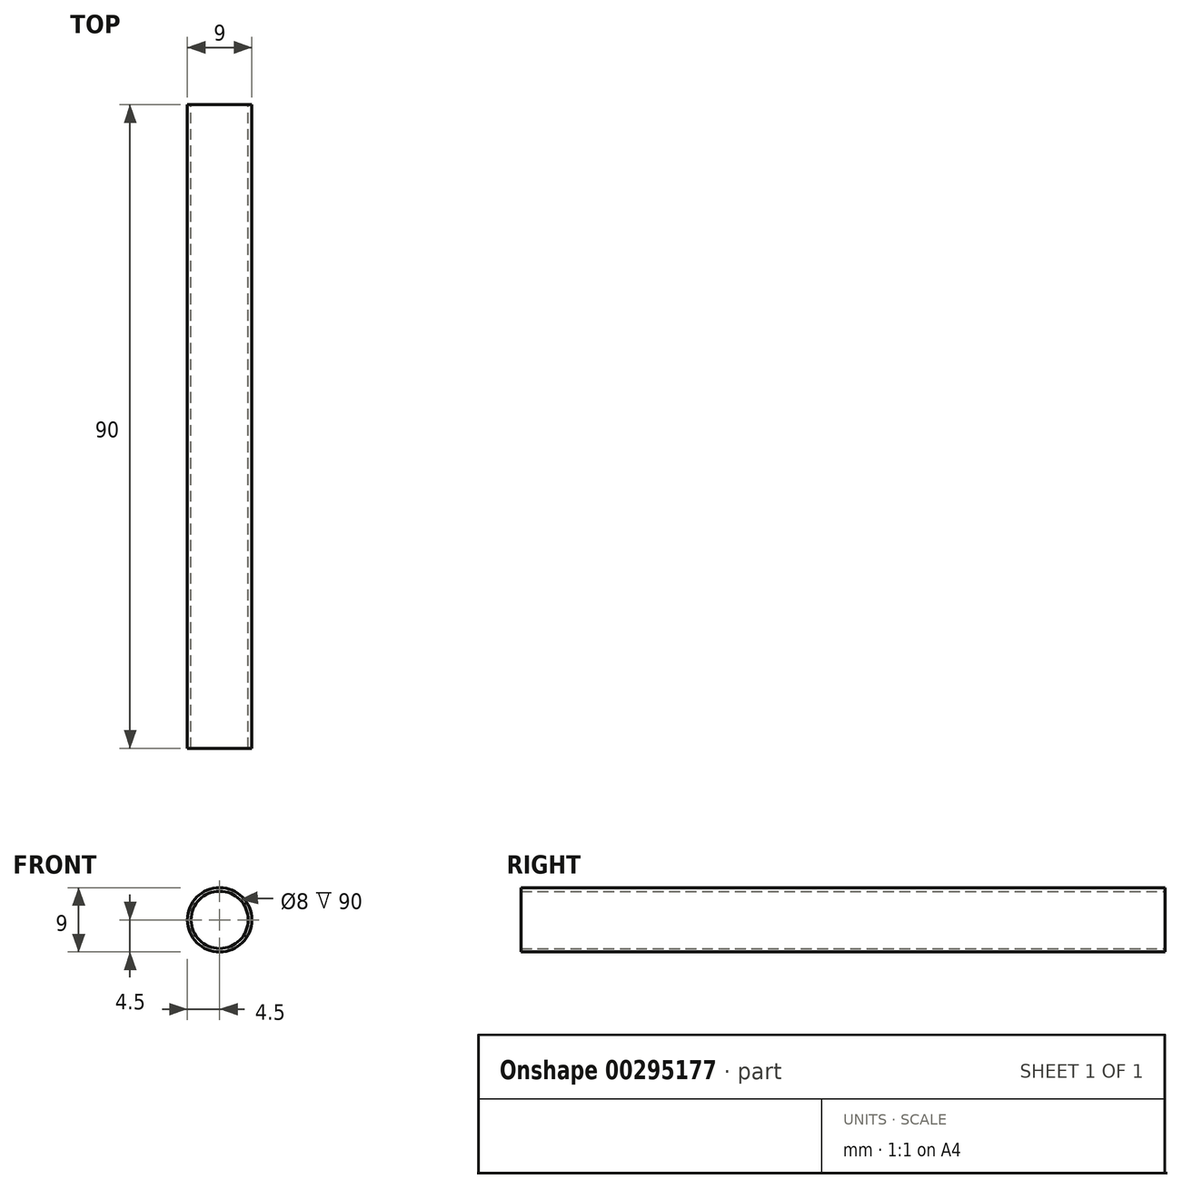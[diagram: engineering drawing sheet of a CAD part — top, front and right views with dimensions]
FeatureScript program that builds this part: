
annotation { "Feature Type Name" : "Feature", "Feature Type Description" : "" }
export const myFeature = defineFeature(function(context is Context, id is Id, definition is map)
    precondition{}
    {
        {
            var Q0;
            Q0=qCreatedBy(makeId("Front.planeOp"),FACE);
            var sketch = newSketch(context, id + "F0", { "sketchPlane" : qUnion([Q0])});
            skCircle(sketch, "E0", {"center": v(0, 0) * mm, "radius": 4.5 * mm});
            skCircle(sketch, "E1", {"center": v(0, 0) * mm, "radius": 4 * mm});
            skSolve(sketch);
        }
        {
            var Q0;
            Q0=makeQuery(id+"F0.imprint","IMPRINT",FACE,{"disambiguationData":[TD([[makeQuery(id+"F0.imprint","IMPRINT",EDGE,{"derivedFrom":sQuery(id+"F0.wireOp",EDGE,"E0")}),1.0]])]});
            extrude(context, id + "F1", {"entities" : qUnion([Q0]), "endBound" : BoundingType.SYMMETRIC, "depth" : 90 * mm});
        }
    });
